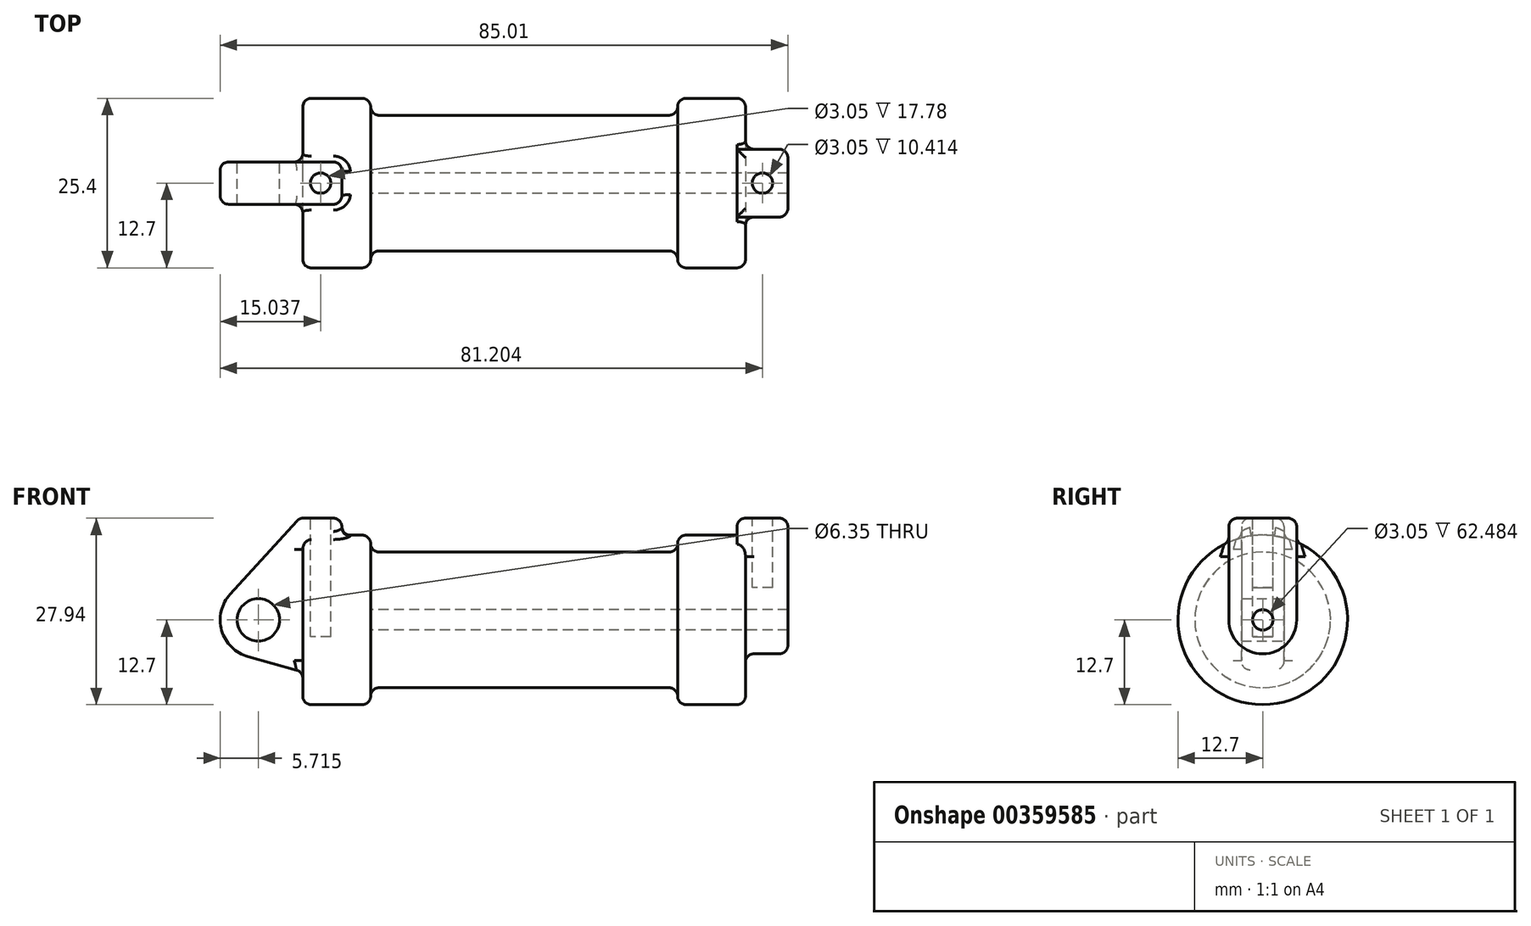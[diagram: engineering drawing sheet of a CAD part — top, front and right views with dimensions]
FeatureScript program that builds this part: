
annotation { "Feature Type Name" : "Feature", "Feature Type Description" : "" }
export const myFeature = defineFeature(function(context is Context, id is Id, definition is map)
    precondition{}
    {
        {
            var Q0;
            Q0=qCreatedBy(makeId("Front.planeOp"),FACE);
            var sketch = newSketch(context, id + "F0", { "sketchPlane" : qUnion([Q0])});
            skLineSegment(sketch, "E0", {"start": v(0, 0) * mm, "end": v(0, 12.7) * mm});
            skLineSegment(sketch, "E1", {"start": v(0, 12.7) * mm, "end": v(10.16, 12.7) * mm});
            skLineSegment(sketch, "E2", {"start": v(10.16, 12.7) * mm, "end": v(10.16, 10.16) * mm});
            skLineSegment(sketch, "E3", {"start": v(10.16, 10.16) * mm, "end": v(56.13, 10.16) * mm});
            skLineSegment(sketch, "E4", {"start": v(56.13, 10.16) * mm, "end": v(56.13, 12.7) * mm});
            skLineSegment(sketch, "E5", {"start": v(56.13, 12.7) * mm, "end": v(66.3, 12.7) * mm});
            skLineSegment(sketch, "E6", {"start": v(66.3, 12.7) * mm, "end": v(66.3, 0) * mm});
            skLineSegment(sketch, "E7", {"start": v(66.3, 0) * mm, "end": v(0, 0) * mm});
            skLineSegment(sketch, "E8", {"start": v(5.84, 15.24) * mm, "end": v(-0.5, 15.24) * mm});
            skLineSegment(sketch, "E9", {"start": v(-0.5, 15.24) * mm, "end": v(-10.88, 3.85) * mm});
            skLineSegment(sketch, "E10", {"start": v(0, 0) * mm, "end": v(-6.65, 0) * mm});
            skCircle(sketch, "E11", {"center": v(-6.65, 0) * mm, "radius": 5.72 * mm});
            skCircle(sketch, "E12", {"center": v(-6.65, 0) * mm, "radius": 3.18 * mm});
            skLineSegment(sketch, "E13", {"start": v(5.84, 15.24) * mm, "end": v(5.84, -9.4) * mm});
            skLineSegment(sketch, "E14", {"start": v(5.84, -9.4) * mm, "end": v(-8.18, -5.5) * mm});
            skSolve(sketch);
        }
        {
            var Q0;
            {var subQ0=sQuery(id+"F0.wireOp",EDGE,"E2");Q0=makeQuery(id+"F0.imprint","IMPRINT",FACE,{"disambiguationData":[TD([[makeQuery(id+"F0.imprint","IMPRINT",EDGE,{"derivedFrom":subQ0}),-1.0]])]});}
            var Q1;
            {var subQ0=sQuery(id+"F0.wireOp",EDGE,"E0");Q1=makeQuery(id+"F0.imprint","IMPRINT",FACE,{"disambiguationData":[TD([[makeQuery(id+"F0.imprint","IMPRINT",EDGE,{"derivedFrom":subQ0}),-1.0]])]});}
            var Q2;
            Q2=sQuery(id+"F0.wireOp",EDGE,"E7");
            revolve(context, id + "F1", {"entities" : qUnion([Q0, Q1]), "axis" : qUnion([Q2]), "revolveType" : RevolveType.FULL});
        }
        {
            var Q0;
            {var subQ3=sQuery(id+"F0.wireOp",EDGE,"E0");Q0=makeQuery(id+"F0.imprint","IMPRINT",FACE,{"disambiguationData":[TD([[makeQuery(id+"F0.imprint","IMPRINT",EDGE,{"derivedFrom":subQ3}),1.0]])]});}
            var Q1;
            {var subQ4=sQuery(id+"F0.wireOp",EDGE,"E12");Q1=makeQuery(id+"F0.imprint","IMPRINT",FACE,{"disambiguationData":[TD([[makeQuery(id+"F0.imprint","IMPRINT",EDGE,{"derivedFrom":subQ4}),-1.0]])]});}
            var Q2;
            {var subQ0=sQuery(id+"F0.wireOp",EDGE,"E14");Q2=makeQuery(id+"F0.imprint","IMPRINT",FACE,{"disambiguationData":[TD([[makeQuery(id+"F0.imprint","IMPRINT",EDGE,{"derivedFrom":subQ0}),-1.0]])]});}
            var Q3;
            {var subQ0=sQuery(id+"F0.wireOp",EDGE,"E0");Q3=makeQuery(id+"F0.imprint","IMPRINT",FACE,{"disambiguationData":[TD([[makeQuery(id+"F0.imprint","IMPRINT",EDGE,{"derivedFrom":subQ0}),-1.0]])]});}
            extrude(context, id + "F2", {"entities" : qUnion([Q0, Q1, Q2, Q3]), "operationType" : NewBodyOperationType.ADD, "endBound" : BoundingType.SYMMETRIC, "depth" : 6.35 * mm});
        }
        {
            var Q0;
            Q0=makeQuery(id+"F1.opRevolve","SWEPT_FACE",FACE,{"disambiguationData":[OSD([sQuery(id+"F0.wireOp",EDGE,"E6")])]});
            var sketch = newSketch(context, id + "F3", { "sketchPlane" : qUnion([Q0])});
            skCircle(sketch, "E15", {"center": v(0, 0) * mm, "radius": 1.52 * mm});
            skCircle(sketch, "E16", {"center": v(0, 0) * mm, "radius": 5.08 * mm});
            skLineSegment(sketch, "E17", {"start": v(-5.08, 0) * mm, "end": v(-5.08, 15.24) * mm});
            skLineSegment(sketch, "E18", {"start": v(-5.08, 15.24) * mm, "end": v(5.08, 15.24) * mm});
            skLineSegment(sketch, "E19", {"start": v(5.08, 15.24) * mm, "end": v(5.08, 0) * mm});
            skSolve(sketch);
        }
        {
            var Q0;
            {var subQ0=sQuery(id+"F3.wireOp",EDGE,"E18");Q0=makeQuery(id+"F3.imprint","IMPRINT",FACE,{"disambiguationData":[TD([[makeQuery(id+"F3.imprint","IMPRINT",EDGE,{"derivedFrom":subQ0}),-1.0]])]});}
            extrude(context, id + "F4", {"entities" : qUnion([Q0]), "operationType" : NewBodyOperationType.ADD, "oppositeDirection" : true, "depth" : 1.27 * mm});
        }
        {
            var Q0;
            {var subQ0=sQuery(id+"F3.wireOp",EDGE,"E18");Q0=makeQuery(id+"F3.imprint","IMPRINT",FACE,{"disambiguationData":[TD([[makeQuery(id+"F3.imprint","IMPRINT",EDGE,{"derivedFrom":subQ0}),-1.0]])]});}
            var Q1;
            {var subQ0=sQuery(id+"F3.wireOp",EDGE,"E17");var subQ1=sQuery(id+"F3.wireOp",EDGE,"E16");var subQ2=makeQuery(id+"F3.imprint","INTERSECT",VERTEX,{"derivedFrom":[subQ1,subQ0]});Q1=makeQuery(id+"F3.imprint","IMPRINT",FACE,{"disambiguationData":[TD([[makeQuery(id+"F3.imprint","IMPRINT",EDGE,{"disambiguationData":[TD([[subQ2,1.0]])],"derivedFrom":subQ1}),-1.0]])]});}
            var Q2;
            Q2=makeQuery(id+"F3.imprint","IMPRINT",FACE,{"disambiguationData":[TD([[makeQuery(id+"F3.imprint","IMPRINT",EDGE,{"derivedFrom":sQuery(id+"F3.wireOp",EDGE,"E15")}),-1.0]])]});
            extrude(context, id + "F5", {"entities" : qUnion([Q0, Q1, Q2]), "operationType" : NewBodyOperationType.ADD, "depth" : 6.35 * mm});
        }
        {
            var Q0;
            Q0=makeQuery(id+"F3.imprint","IMPRINT",FACE,{"disambiguationData":[TD([[makeQuery(id+"F3.imprint","IMPRINT",EDGE,{"derivedFrom":sQuery(id+"F3.wireOp",EDGE,"E15")}),1.0]])]});
            var Q1;
            Q1=makeQuery(id+"F1.opRevolve","SWEPT_FACE",FACE,{"disambiguationData":[OSD([sQuery(id+"F0.wireOp",EDGE,"E2")])]});
            extrude(context, id + "F6", {"entities" : qUnion([Q0]), "operationType" : NewBodyOperationType.REMOVE, "endBound" : BoundingType.UP_TO_SURFACE, "oppositeDirection" : true, "endBoundEntityFace" : qUnion([Q1]), "depth" : 25.4 * mm});
        }
        {
            var Q0;
            Q0=makeQuery(id+"F2.opExtrude","SWEPT_FACE",FACE,{"disambiguationData":[OSD([sQuery(id+"F0.wireOp",EDGE,"E8")])]});
            var sketch = newSketch(context, id + "F7", { "sketchPlane" : qUnion([Q0])});
            skCircle(sketch, "E20", {"center": v(2.67, 0) * mm, "radius": 1.52 * mm});
            skPoint(sketch, "E20.centerSnap0", {"position": v(-0.5, 0) * mm});
            skPoint(sketch, "E20.centerSnap1", {"position": v(2.67, 3.18) * mm});
            skSolve(sketch);
        }
        {
            var Q0;
            Q0=qSketchRegion(id+"F7",true);
            extrude(context, id + "F8", {"entities" : qUnion([Q0]), "operationType" : NewBodyOperationType.REMOVE, "oppositeDirection" : true, "depth" : 17.78 * mm});
        }
        {
            var Q0;
            {var subQ0=sQuery(id+"F3.wireOp",EDGE,"E18");Q0=makeQuery(id+"F5.boolean.opBoolean","MERGE",FACE,{"derivedFrom":[makeQuery(id+"F4.opExtrude","SWEPT_FACE",FACE,{"disambiguationData":[OSD([subQ0])]}),makeQuery(id+"F5.opExtrude","SWEPT_FACE",FACE,{"disambiguationData":[OSD([subQ0])]})]});}
            var sketch = newSketch(context, id + "F9", { "sketchPlane" : qUnion([Q0])});
            skCircle(sketch, "E21", {"center": v(68.83, 0) * mm, "radius": 1.52 * mm});
            skPoint(sketch, "E21.centerSnap0", {"position": v(65.02, 0) * mm});
            skPoint(sketch, "E21.centerSnap1", {"position": v(68.83, 5.08) * mm});
            skSolve(sketch);
        }
        {
            var Q0;
            Q0=qSketchRegion(id+"F9",true);
            extrude(context, id + "F10", {"entities" : qUnion([Q0]), "operationType" : NewBodyOperationType.REMOVE, "oppositeDirection" : true, "depth" : 10.4 * mm});
        }
        {
            var Q0;
            Q0=makeQuery(id+"F1.opRevolve","SWEPT_EDGE",EDGE,{"disambiguationData":[OSD([sQuery(id+"F0.wireOp",EDGE,"E2"),sQuery(id+"F0.wireOp",EDGE,"E3")])]});
            var Q1;
            Q1=makeQuery(id+"F1.opRevolve","SWEPT_EDGE",EDGE,{"disambiguationData":[OSD([sQuery(id+"F0.wireOp",EDGE,"E1"),sQuery(id+"F0.wireOp",EDGE,"E2")])]});
            var Q2;
            Q2=makeQuery(id+"F1.opRevolve","SWEPT_EDGE",EDGE,{"disambiguationData":[OSD([sQuery(id+"F0.wireOp",EDGE,"E3"),sQuery(id+"F0.wireOp",EDGE,"E4")])]});
            var Q3;
            Q3=makeQuery(id+"F1.opRevolve","SWEPT_EDGE",EDGE,{"disambiguationData":[OSD([sQuery(id+"F0.wireOp",EDGE,"E4"),sQuery(id+"F0.wireOp",EDGE,"E5")])]});
            var Q4;
            Q4=makeQuery(id+"F1.opRevolve","SWEPT_EDGE",EDGE,{"disambiguationData":[OSD([sQuery(id+"F0.wireOp",EDGE,"E5"),sQuery(id+"F0.wireOp",EDGE,"E6")])]});
            var Q5;
            Q5=makeQuery(id+"F1.opRevolve","SWEPT_EDGE",EDGE,{"disambiguationData":[OSD([sQuery(id+"F0.wireOp",EDGE,"E0"),sQuery(id+"F0.wireOp",EDGE,"E1")])]});
            fillet(context, id + "F11", {"entities" : qUnion([Q0, Q1, Q2, Q3, Q4, Q5]), "radius" : 1.27 * mm, "tangentPropagation" : true, "allowEdgeOverflow" : false});
        }
        {
            var Q0;
            Q0=makeQuery(id+"F1.boolean.opBoolean","INTERSECT",EDGE,{"derivedFrom":[makeQuery(id+"F2.opExtrude","CAP_FACE",FACE,{"disambiguationData":[OSD([sQuery(id+"F0.wireOp",EDGE,"E8"),sQuery(id+"F0.wireOp",EDGE,"E9"),sQuery(id+"F0.wireOp",EDGE,"E11"),sQuery(id+"F0.wireOp",EDGE,"E12"),sQuery(id+"F0.wireOp",EDGE,"E13"),sQuery(id+"F0.wireOp",EDGE,"E14")])],"isStart":false}),makeQuery(id+"F1.opRevolve","SWEPT_FACE",FACE,{"disambiguationData":[OSD([sQuery(id+"F0.wireOp",EDGE,"E1")])]})]});
            var Q1;
            Q1=makeQuery(id+"F1.opRevolve","SWEPT_FACE",FACE,{"disambiguationData":[OSD([sQuery(id+"F0.wireOp",EDGE,"E0")])]});
            var Q2;
            Q2=makeQuery(id+"F2.opExtrude","CAP_EDGE",EDGE,{"disambiguationData":[OSD([sQuery(id+"F0.wireOp",EDGE,"E9")])],"isStart":true});
            var Q3;
            Q3=makeQuery(id+"F2.opExtrude","CAP_EDGE",EDGE,{"disambiguationData":[OSD([sQuery(id+"F0.wireOp",EDGE,"E9")])],"isStart":false});
            var Q4;
            Q4=makeQuery(id+"F5.opExtrude","CAP_EDGE",EDGE,{"disambiguationData":[OSD([sQuery(id+"F3.wireOp",EDGE,"E17")])],"isStart":true});
            var Q5;
            Q5=makeQuery(id+"F5.opExtrude","CAP_EDGE",EDGE,{"disambiguationData":[OSD([sQuery(id+"F3.wireOp",EDGE,"E17")])],"isStart":false});
            var Q6;
            {var subQ0=sQuery(id+"F3.wireOp",EDGE,"E18");var subQ1=sQuery(id+"F3.wireOp",EDGE,"E17");Q6=makeQuery(id+"F5.boolean.opBoolean","MERGE",EDGE,{"derivedFrom":[makeQuery(id+"F4.opExtrude","SWEPT_EDGE",EDGE,{"disambiguationData":[OSD([subQ1,subQ0])]}),makeQuery(id+"F5.opExtrude","SWEPT_EDGE",EDGE,{"disambiguationData":[OSD([subQ1,subQ0])]})]});}
            var Q7;
            {var subQ0=sQuery(id+"F3.wireOp",EDGE,"E19");var subQ1=sQuery(id+"F3.wireOp",EDGE,"E18");Q7=makeQuery(id+"F5.boolean.opBoolean","MERGE",EDGE,{"derivedFrom":[makeQuery(id+"F4.opExtrude","SWEPT_EDGE",EDGE,{"disambiguationData":[OSD([subQ1,subQ0])]}),makeQuery(id+"F5.opExtrude","SWEPT_EDGE",EDGE,{"disambiguationData":[OSD([subQ1,subQ0])]})]});}
            var Q8;
            Q8=makeQuery(id+"F4.opExtrude","CAP_EDGE",EDGE,{"disambiguationData":[OSD([sQuery(id+"F3.wireOp",EDGE,"E18")])],"isStart":false});
            var Q9;
            Q9=makeQuery(id+"F5.opExtrude","CAP_EDGE",EDGE,{"disambiguationData":[OSD([sQuery(id+"F3.wireOp",EDGE,"E18")])],"isStart":false});
            var Q10;
            Q10=makeQuery(id+"F2.opExtrude","CAP_EDGE",EDGE,{"disambiguationData":[OSD([sQuery(id+"F0.wireOp",EDGE,"E8")])],"isStart":false});
            var Q11;
            Q11=makeQuery(id+"F2.opExtrude","SWEPT_EDGE",EDGE,{"disambiguationData":[OSD([sQuery(id+"F0.wireOp",EDGE,"E8"),sQuery(id+"F0.wireOp",EDGE,"E9")])]});
            var Q12;
            Q12=makeQuery(id+"F2.opExtrude","CAP_EDGE",EDGE,{"disambiguationData":[OSD([sQuery(id+"F0.wireOp",EDGE,"E8")])],"isStart":true});
            var Q13;
            Q13=makeQuery(id+"F2.opExtrude","SWEPT_EDGE",EDGE,{"disambiguationData":[OSD([sQuery(id+"F0.wireOp",EDGE,"E8"),sQuery(id+"F0.wireOp",EDGE,"E13")])]});
            var Q14;
            Q14=makeQuery(id+"F2.opExtrude","SWEPT_FACE",FACE,{"disambiguationData":[OSD([sQuery(id+"F0.wireOp",EDGE,"E13")])]});
            var Q15;
            Q15=makeQuery(id+"F4.opExtrude","CAP_EDGE",EDGE,{"disambiguationData":[OSD([sQuery(id+"F0.wireOp",EDGE,"E5"),sQuery(id+"F0.wireOp",EDGE,"E6")])],"isStart":false});
            fillet(context, id + "F12", {"entities" : qUnion([Q0, Q1, Q2, Q3, Q4, Q5, Q6, Q7, Q8, Q9, Q10, Q11, Q12, Q13, Q14, Q15]), "radius" : 1.27 * mm, "tangentPropagation" : true, "allowEdgeOverflow" : false});
        }
    });
